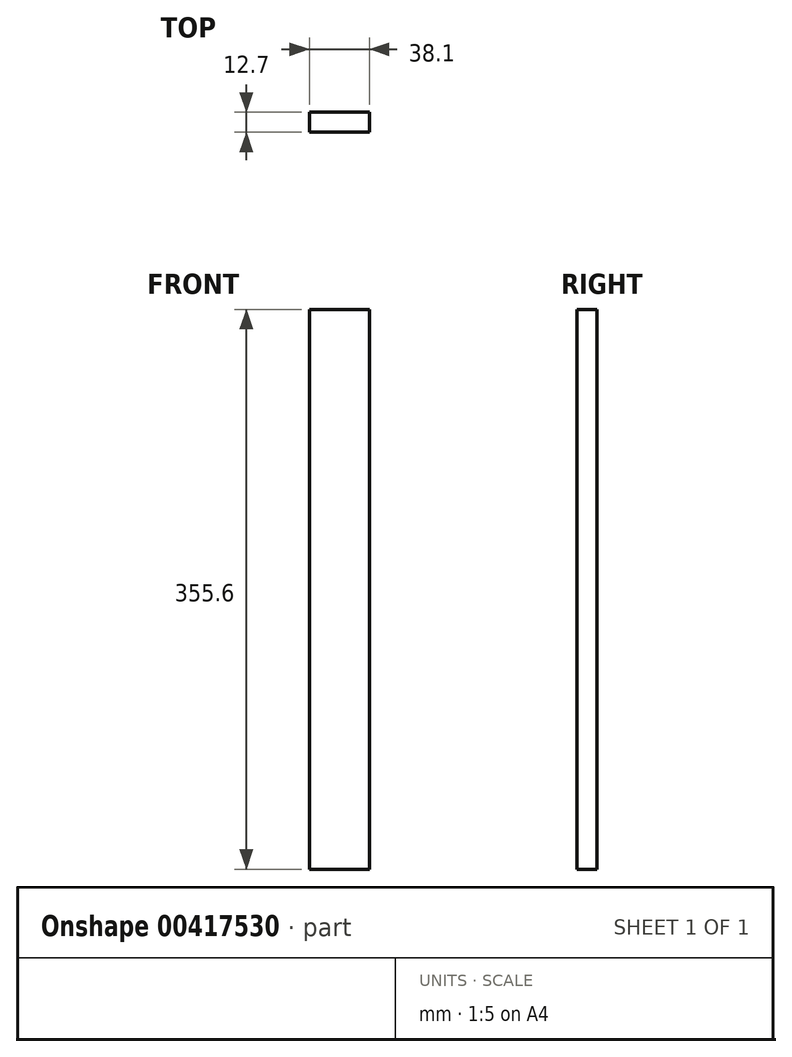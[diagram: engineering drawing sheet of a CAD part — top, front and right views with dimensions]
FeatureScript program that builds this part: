
annotation { "Feature Type Name" : "Feature", "Feature Type Description" : "" }
export const myFeature = defineFeature(function(context is Context, id is Id, definition is map)
    precondition{}
    {
        {
            var Q0;
            Q0=qCreatedBy(makeId("Front.planeOp"),FACE);
            var sketch = newSketch(context, id + "F0", { "sketchPlane" : qUnion([Q0])});
            skLineSegment(sketch, "E0.bottom", {"start": v(-19.05, 177.8) * mm, "end": v(19.05, 177.8) * mm});
            skLineSegment(sketch, "E0.top", {"start": v(-19.05, -177.8) * mm, "end": v(19.05, -177.8) * mm});
            skLineSegment(sketch, "E0.left", {"start": v(-19.05, 177.8) * mm, "end": v(-19.05, -177.8) * mm});
            skLineSegment(sketch, "E0.right", {"start": v(19.05, 177.8) * mm, "end": v(19.05, -177.8) * mm});
            skPoint(sketch, "E0.middle", {"position": v(0, 0) * mm});
            skSolve(sketch);
        }
        {
            var Q0;
            Q0 = qSketchRegion(id + "F0", true);
            extrude(context, id + "F1", {"entities" : qUnion([Q0]), "depth" : 12.7 * mm});
        }
    });
